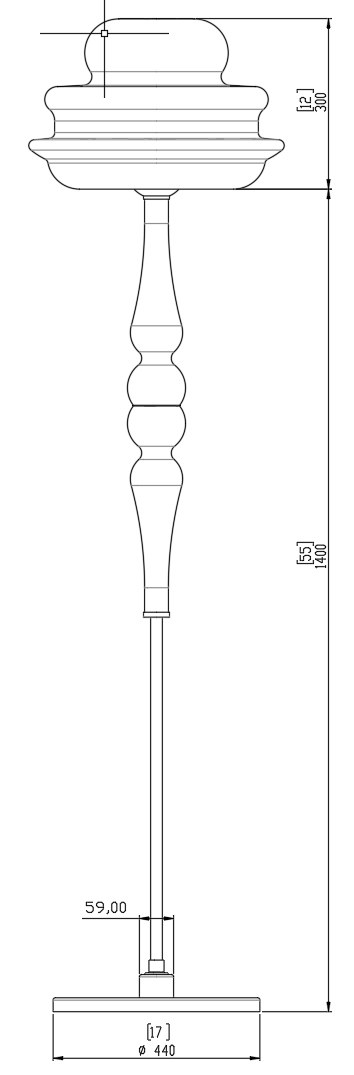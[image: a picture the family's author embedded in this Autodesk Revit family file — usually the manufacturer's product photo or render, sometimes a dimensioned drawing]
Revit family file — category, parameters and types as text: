
# Revit family: NOVECENTO-Celling
name_source: partatom
category: Lighting Fixtures
units: mm (PartAtom-declared; Revit-internal decimal feet)

## family parameters
Always vertical = Yes
Cut with Voids When Loaded = No
Host = Ceiling
Light Source = No
OmniClass Number = 23.80.70.11
OmniClass Title = Luminaries for Internal Lighting
Part Type = Normal
Room Calculation Point = No
Round Connector Dimension = Use Diameter
Shared = No

## types (1)
- NOVACENTO PL
    Bulb Diametr = 15 mm  [stored 0.0492126 ft]
    Country = Europe
    Default Elevation = 0 mm  [stored 0 ft]
    Depth = 41 mm  [stored 0.134514 ft]
    Description = CEILING LAMP
    Designer = Studio Debonademeo
    Manufacturer = Vistosi
    Manufacturer country = Italy
    Model = NOVECENTO
    Type Comments = Studio Debonademeo
    URL = https://vistosi.com
    URL Product Page = https://vistosi.it
    Width = 54 mm  [stored 0.177165 ft]

note: [stored X ft] marks values corroborated as IEEE doubles in the binary element streams (Revit-internal decimal feet)

## geometry (parser evidence)
native form markers: Sweep x8
no freeform markers — native parametric forms only
